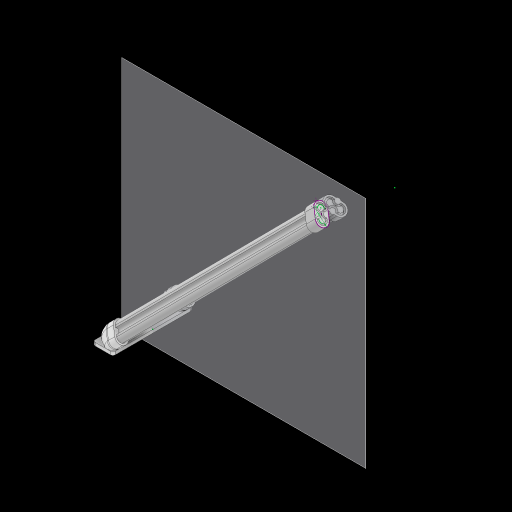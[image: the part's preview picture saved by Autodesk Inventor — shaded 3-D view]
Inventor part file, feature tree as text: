
AUTODESK INVENTOR PART (.ipt)
format: ipt  version: 2023 (Build 270158000, 158)  size: 483,328 bytes
history: native  units: mm
features: sketch x8, extrude x5, plane x4, chamfer x3, sweep x1, fillet x1, revolve x1, mirror x1
ambient origin geometry x8: Origin, YZ Plane, XZ Plane, XY Plane, X Axis, Y Axis, Z Axis, Center Point
bodies: Solid1 (feature_tree)
feature tree (24):
  sketch  "Sketch1"  dims[d0=100.0mm d1=25.0mm d2=7.5mm d3=7.5mm d4=60.0deg d5=15.0mm d6=11.0mm d7=11.0mm d8=15.0mm d11=135.0deg]
  plane  "Work Plane1"
  sweep  "Sweep1"
  extrude  "Extrusion1"  Depth=4.0mm TaperAngle=0.0deg
  fillet  "Fillet1"  Radius=3.0mm
  revolve  "Revolution1"  Angle=45.0deg
  sketch  "Sketch6"  dims[d31=10.0mm d32=9.948377mm]
  extrude  "Extrusion3"  Depth=10.0mm
  chamfer  "Chamfer2"  Distance=0.959931mm
  extrude  "Extrusion4"  Depth=10.0mm
  mirror  "Mirror3"
  chamfer  "Chamfer3"  Distance=11.0mm
  chamfer  "Chamfer4"  Distance=2.0mm
  plane  "Work Plane2"
  sketch  "Sketch8"  dims[d33=10.0mm]
  plane  "Work Plane3"
  extrude  "Extrusion5"  Depth=10.0mm
  extrude  "Extrusion6"  Depth=10.0mm
  sketch  "Sketch10"  dims[d35=9.948377mm]
  plane  "Work Plane9"
  sketch  "Sketch13"  dims[d37=10.0mm d38=0.959931mm d44=11.0mm d48=11.0mm d49=2.0mm d50=6.5mm d51=6.5mm d52=10.0mm d53=0.0mm d54=2.0mm d55=4.0mm d56=45.0deg d57=325.0mm d58=0.0mm d59=2.0mm d60=4.0mm d61=45.0deg d62=2.0mm d63=4.0mm d64=45.0deg d81=7.5mm d82=7.5mm d85=11.0mm d86=11.0mm d87=2.0mm d88=6.5mm d89=6.5mm d90=7.5mm d91=7.5mm d92=11.0mm d93=11.0mm d94=2.0mm d95=6.5mm d96=6.5mm d97=4.0mm d98=0.0mm d99=4.0mm d100=0.0mm d101=10.0mm d102=0.0mm d103=10.0mm d104=0.0mm d105=15.0mm]
  sketch  "Sketch3"  dims[d12=0.0mm d13=0.0mm d14=4.0mm d15=0.0mm d28=3.0mm]
  sketch  "Sketch5"  dims[d29=11.389087mm d30=45.0deg]
  sketch  "Sketch9"  dims[d34=10.0mm]
